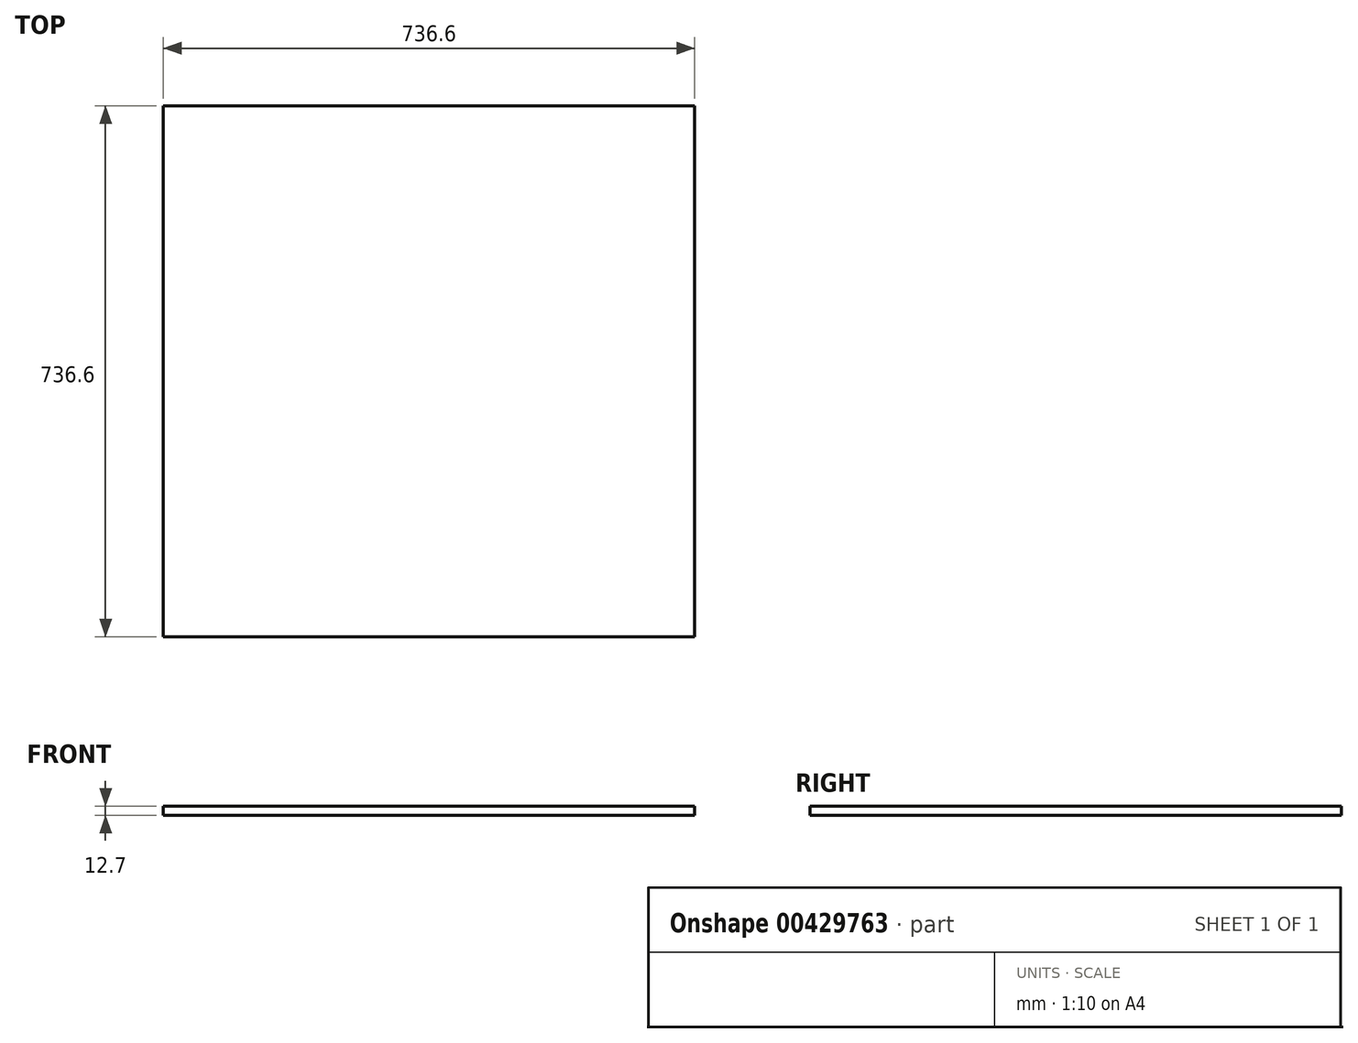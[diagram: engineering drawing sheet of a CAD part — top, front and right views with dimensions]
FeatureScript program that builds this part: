
annotation { "Feature Type Name" : "Feature", "Feature Type Description" : "" }
export const myFeature = defineFeature(function(context is Context, id is Id, definition is map)
    precondition{}
    {
        {
            var Q0;
            Q0=qCreatedBy(makeId("Top.planeOp"),FACE);
            var sketch = newSketch(context, id + "F0", { "sketchPlane" : qUnion([Q0])});
            skLineSegment(sketch, "E0.bottom", {"start": v(368.3, 368.3) * mm, "end": v(-368.3, 368.3) * mm});
            skLineSegment(sketch, "E0.top", {"start": v(368.3, -368.3) * mm, "end": v(-368.3, -368.3) * mm});
            skLineSegment(sketch, "E0.left", {"start": v(368.3, 368.3) * mm, "end": v(368.3, -368.3) * mm});
            skLineSegment(sketch, "E0.right", {"start": v(-368.3, 368.3) * mm, "end": v(-368.3, -368.3) * mm});
            skPoint(sketch, "E0.middle", {"position": v(0, 0) * mm});
            skSolve(sketch);
        }
        {
            var Q0;
            Q0 = qSketchRegion(id + "F0", true);
            extrude(context, id + "F1", {"entities" : qUnion([Q0]), "depth" : 12.7 * mm});
        }
    });
